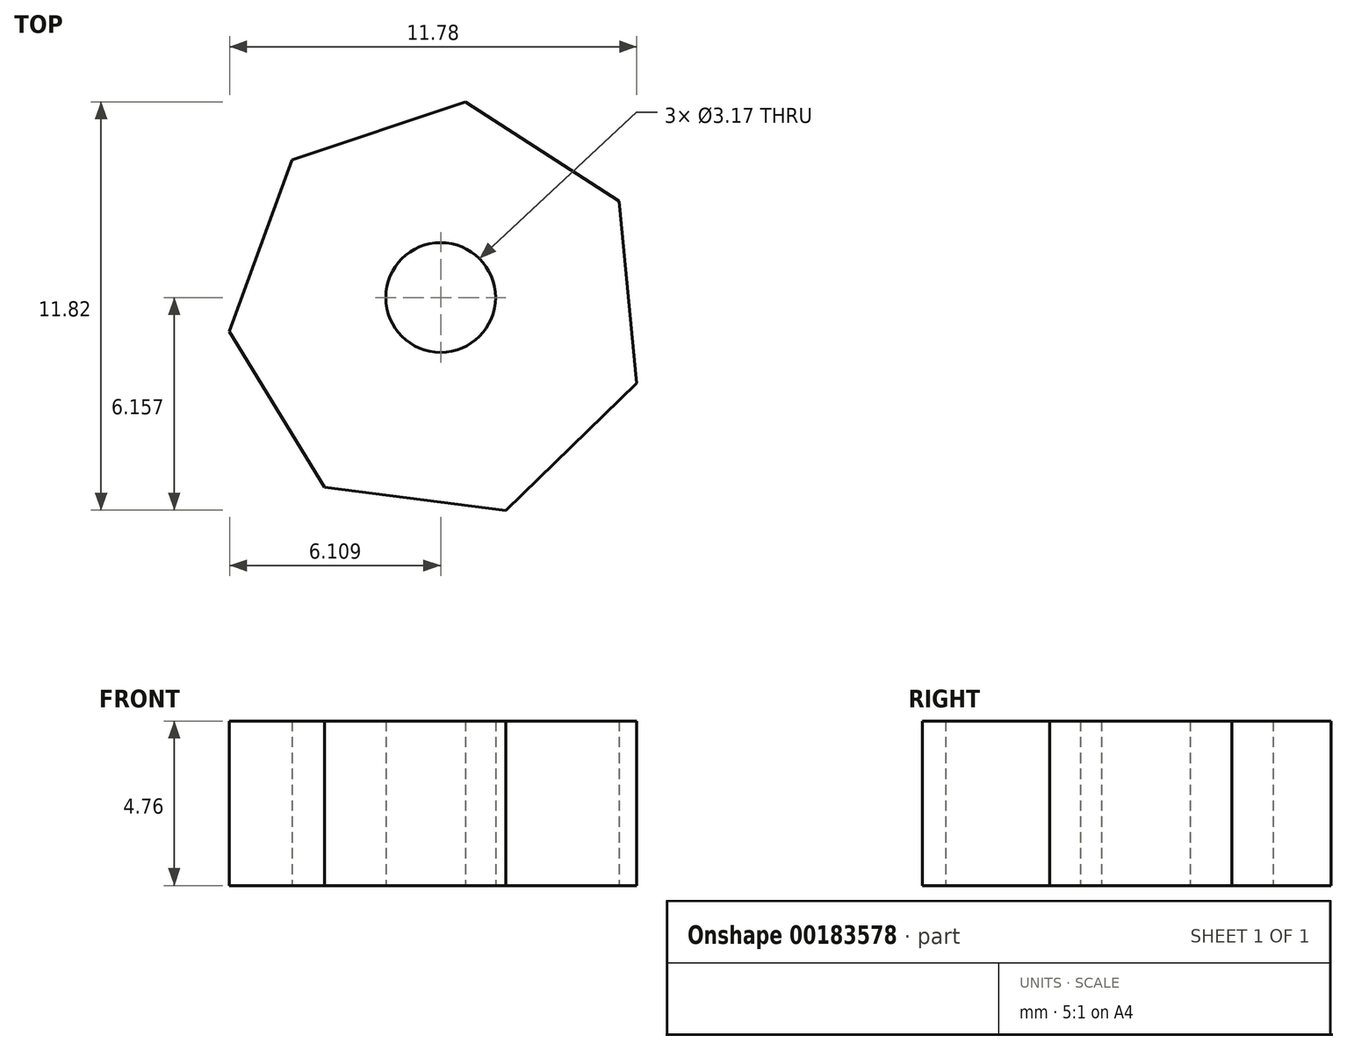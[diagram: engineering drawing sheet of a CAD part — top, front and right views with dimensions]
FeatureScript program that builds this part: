
annotation { "Feature Type Name" : "Feature", "Feature Type Description" : "" }
export const myFeature = defineFeature(function(context is Context, id is Id, definition is map)
    precondition{}
    {
        {
            var Q0;
            Q0=qCreatedBy(makeId("Top.planeOp"),FACE);
            var sketch = newSketch(context, id + "F0", { "sketchPlane" : qUnion([Q0])});
            skCircle(sketch, "E0.cCircle", {"center": v(8.32, 22.1) * mm, "radius": 5.49 * mm, "construction": true});
            skLineSegment(sketch, "E0.0", {"start": v(5, 17) * mm, "end": v(2.26, 21.51) * mm});
            skLineSegment(sketch, "E0.1", {"start": v(2.26, 21.51) * mm, "end": v(4.07, 26.47) * mm});
            skLineSegment(sketch, "E0.2", {"start": v(4.07, 26.47) * mm, "end": v(9.09, 28.15) * mm});
            skLineSegment(sketch, "E0.3", {"start": v(9.09, 28.15) * mm, "end": v(13.52, 25.27) * mm});
            skLineSegment(sketch, "E0.4", {"start": v(13.52, 25.27) * mm, "end": v(14.04, 20.01) * mm});
            skLineSegment(sketch, "E0.5", {"start": v(14.04, 20.01) * mm, "end": v(10.25, 16.33) * mm});
            skLineSegment(sketch, "E0.6", {"start": v(10.25, 16.33) * mm, "end": v(5, 17) * mm});
            skPoint(sketch, "E0.0.midPoint", {"position": v(3.63, 19.25) * mm});
            skSolve(sketch);
        }
        {
            var Q0;
            Q0=qCreatedBy(makeId("Top.planeOp"),FACE);
            var sketch = newSketch(context, id + "F1", { "sketchPlane" : qUnion([Q0])});
            skSolve(sketch);
        }
        {
            var Q0;
            Q0 = qSketchRegion(id + "F1", true);
            var Q1;
            Q1=makeQuery(id+"F0.imprint","IMPRINT",FACE,{"disambiguationData":[TD([[makeQuery(id+"F0.imprint","IMPRINT",EDGE,{"derivedFrom":sQuery(id+"F0.wireOp",EDGE,"E0.0")}),-1.0]])]});
            extrude(context, id + "F2", {"entities" : qUnion([Q0, Q1]), "depth" : 4.76 * mm});
        }
        {
            var Q0;
            Q0=qCreatedBy(makeId("Top.planeOp"),FACE);
            var sketch = newSketch(context, id + "F3", { "sketchPlane" : qUnion([Q0])});
            skCircle(sketch, "E1", {"center": v(8.37, 22.49) * mm, "radius": 1.59 * mm});
            skSolve(sketch);
        }
        {
            var Q0;
            Q0=makeQuery(id+"F2.opExtrude","CAP_FACE",FACE,{"disambiguationData":[OSD([sQuery(id+"F0.wireOp",EDGE,"E0.0"),sQuery(id+"F0.wireOp",EDGE,"E0.1"),sQuery(id+"F0.wireOp",EDGE,"E0.2"),sQuery(id+"F0.wireOp",EDGE,"E0.3"),sQuery(id+"F0.wireOp",EDGE,"E0.4"),sQuery(id+"F0.wireOp",EDGE,"E0.5"),sQuery(id+"F0.wireOp",EDGE,"E0.6")])],"isStart":false});
            var sketch = newSketch(context, id + "F4", { "sketchPlane" : qUnion([Q0])});
            skSolve(sketch);
        }
        {
            var Q0;
            Q0 = qSketchRegion(id + "F4", true);
            var Q1;
            Q1=makeQuery(id+"F3.imprint","IMPRINT",FACE,{"disambiguationData":[TD([[makeQuery(id+"F3.imprint","IMPRINT",EDGE,{"derivedFrom":sQuery(id+"F3.wireOp",EDGE,"E1")}),1.0]])]});
            extrude(context, id + "F5", {"entities" : qUnion([Q0, Q1]), "operationType" : NewBodyOperationType.REMOVE, "depth" : 39.88 * mm});
        }
    });
